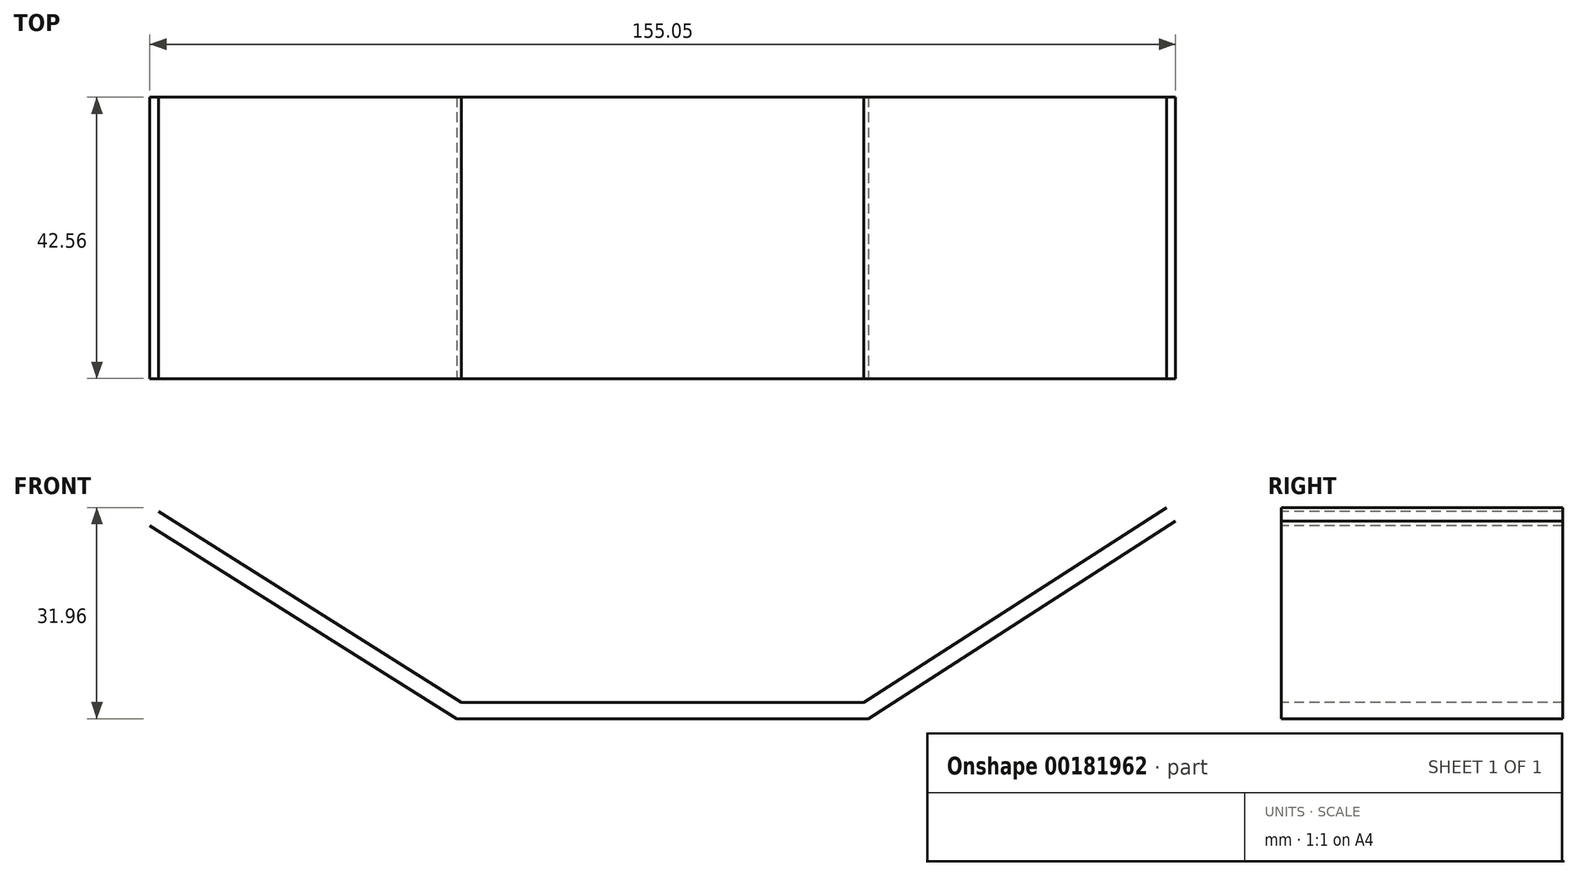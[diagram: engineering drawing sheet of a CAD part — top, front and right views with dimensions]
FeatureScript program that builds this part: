
annotation { "Feature Type Name" : "Feature", "Feature Type Description" : "" }
export const myFeature = defineFeature(function(context is Context, id is Id, definition is map)
    precondition{}
    {
        {
            var Q0;
            Q0=qCreatedBy(makeId("Front.planeOp"),FACE);
            var sketch = newSketch(context, id + "F0", { "sketchPlane" : qUnion([Q0])});
            skLineSegment(sketch, "E0", {"start": v(-30.3, 0) * mm, "end": v(30.52, 0) * mm});
            skLineSegment(sketch, "E1", {"start": v(30.52, 0) * mm, "end": v(-30.3, 0) * mm});
            skLineSegment(sketch, "E2", {"start": v(-30.3, 0) * mm, "end": v(-76.08, 28.84) * mm});
            skLineSegment(sketch, "E3", {"start": v(-76.08, 28.84) * mm, "end": v(-30.3, 0) * mm});
            skLineSegment(sketch, "E4", {"start": v(30.52, 0) * mm, "end": v(76.3, 29.47) * mm});
            skLineSegment(sketch, "E5.0", {"start": v(31.25, -2.49) * mm, "end": v(77.64, 27.38) * mm});
            skLineSegment(sketch, "E5.1", {"start": v(31.25, -2.49) * mm, "end": v(-31.03, -2.49) * mm});
            skLineSegment(sketch, "E5.2", {"start": v(-77.4, 26.74) * mm, "end": v(-31.03, -2.49) * mm});
            skSolve(sketch);
        }
        {
            var Q0;
            Q0=sQuery(id+"F0.wireOp",EDGE,"E4");
            var Q1;
            Q1=sQuery(id+"F0.wireOp",EDGE,"E1");
            var Q2;
            Q2=sQuery(id+"F0.wireOp",EDGE,"E5.2");
            var Q3;
            Q3=sQuery(id+"F0.wireOp",EDGE,"E5.0");
            var Q4;
            Q4=sQuery(id+"F0.wireOp",EDGE,"E3");
            var Q5;
            Q5=sQuery(id+"F0.wireOp",EDGE,"E5.1");
            extrude(context, id + "F1", {"bodyType" : ToolBodyType.SURFACE, "surfaceEntities" : qUnion([Q0, Q1, Q2, Q3, Q4, Q5]), "depth" : 42.56 * mm});
        }
    });
